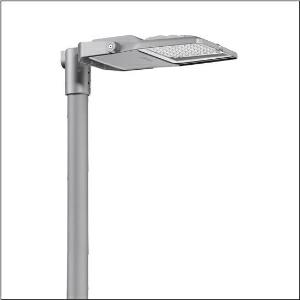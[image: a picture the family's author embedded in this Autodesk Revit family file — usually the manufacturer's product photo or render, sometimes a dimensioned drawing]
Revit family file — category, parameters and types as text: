
# Revit family: floodlight_fl_21_mini___pl64_5xa7775d2e3a_010e
name_source: partatom
category: Lighting Fixtures
units: mm (PartAtom-declared; Revit-internal decimal feet)

## family parameters
Cut with Voids When Loaded = No
Host = Face
Light Source = No
Part Type = Normal
Room Calculation Point = No
Round Connector Dimension = Use Diameter
Shared = No

## types (1)
- --- (1 x LED, 17220 lm, 142.9 W, 3000K)
    Apparent Load = 143 VA
    CIE Flux Codes = 28 80 98 100 100
    Color Rendering = 70
    Color Temperature = 3000K
    Default Elevation = 1800 mm
    Description = Floodlight FL 21 mini, floodlight, primary light control with lens, of PMMA, primary optical cover: protective disc, of toughened safety glass, transparent, light distribution: PL64, light emission: direct distribution, installation type: surface-mounted, LED, High Power LED, rated luminous flux: 17.220lm, luminous efficacy: 121lm/W, light colour: 730, colour temperature: 3000K, control: flexible luminous flux parameterisation, time-dependent luminous flux control, constant luminous flux control, overheat protection, presetting dimming logarithmic, with terminal, 6-pole, mains connection: 220..240V, AC, 50/60Hz, start of lifetime: 143W, end of service life: 151W, reduction: 63W, luminaire housing, of diecast aluminium, powder-coated, Siteco® metallic grey (DB 702S), corrosivity category C5 mid according to DIN EN ISO 12944, sealing non-destructively replaceable, please order mast flange separately, mast bracket, of steel, galvanised, powder-coated, Siteco® metallic grey (DB 702S), Smart Interface above, protection rating (complete): IP66, insulation class (complete): insulation class II (safety insulation), certification: CE, ENEC, VDE, protection symbol: D, impact resistance: IK08, permissible operating ambient temperature: -40..+40°C, permissible operating ambient temperature for outdoor applications: -40..+50°C, standard: DIN EN 12944, LABS conformity tested according to VDMA 24364:2018-05, packaging unit: 1 piece

Light Distribution: PL64
    Height = 70 mm
    Lamp = 1 x LED
    Lamp Light Flux = 17220 lm
    Lamp Power = 142.9 W
    Lamp count = 1
    Length = 485 mm
    Luminous efficacy = 121 lm/W
    Manufacturer = Siteco
    ModVariant = No
    Model = 5XA7775D2E3A
    Number of Poles = 1
    OnlyDefault = Yes
    Power Factor = 1
    Product Name = Floodlight FL 21 mini | PL64
    Product group = floodlight | pylon annexe
    ProductGroupID = 6200
    Protection Class = Protection class II
    Protection Degree = IP 66
    RLX_Detail_Level = 1
    RLX_Emergency_Light_Flux = 0 lm
    RLX_Emergency_Type = 0
    RLX_Emergency_Type_DB = No
    RlxData = <blob elided: 101321 chars, md5=a58de176>
    Socket = socket
    Standby Power = 0 W
    System Light Flux = 17220 lm
    System Power = 143 W
    Type Comments = factory setting: luminous flux: 100 % | dim-lin: 254 | 730 mA
    Type Image = l_1007125.jpg
    URL = http://relux.com
    VarID = @adj_115427
    Voltage = 0 V
    Weight = 0.00 kg
    Width = 337 mm

## geometry (parser evidence)
native form markers: Blend x4, Sweep x13
no freeform markers — native parametric forms only
